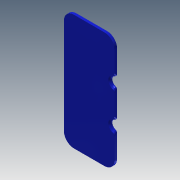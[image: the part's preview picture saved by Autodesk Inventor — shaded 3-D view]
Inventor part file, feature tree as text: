
AUTODESK INVENTOR PART (.ipt)
format: ipt  version: 2013 (Build 170138000, 138)  size: 173,568 bytes
history: native  units: mm
features: extrude x2, fillet x2, sketch x2, chamfer x1
ambient origin geometry x8: Origin, YZ Plane, XZ Plane, XY Plane, X Axis, Y Axis, Z Axis, Center Point
bodies: Solid1 (feature_tree)
feature tree (7):
  extrude  "Extrusion1"  Depth=101.2mm
  fillet  "Fillet1"  Radius=5.0mm
  extrude  "Extrusion2"  Depth=5.0mm TaperAngle=0.0deg
  chamfer  "Chamfer1"  Distance=3.0mm Angle=45.0deg
  fillet  "Fillet2"  Radius=4.0mm
  sketch  "Sketch1"  dims[d0=231.3mm d1=101.2mm d2=5.0mm d3=0.0mm]
  sketch  "Sketch2"  dims[d4=20.0mm d8=5.0mm d9=0.0mm d10=3.0mm d11=2.0mm d12=45.0deg d13=4.0mm]
